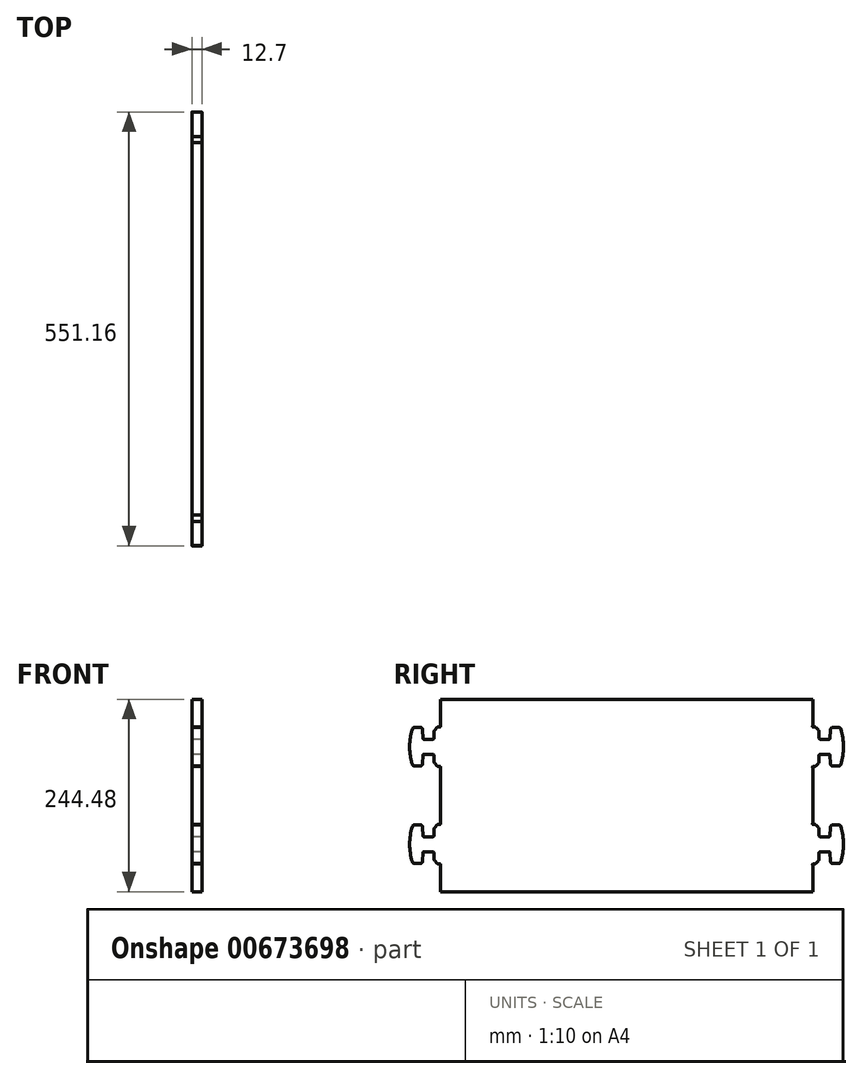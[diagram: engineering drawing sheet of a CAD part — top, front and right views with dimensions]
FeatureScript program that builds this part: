
annotation { "Feature Type Name" : "Feature", "Feature Type Description" : "" }
export const myFeature = defineFeature(function(context is Context, id is Id, definition is map)
    precondition{}
    {
        {
            var Q0;
            Q0=qCreatedBy(makeId("Right.planeOp"),FACE);
            var sketch = newSketch(context, id + "F0", { "sketchPlane" : qUnion([Q0])});
            skLineSegment(sketch, "E0", {"start": v(236.54, -75.4) * mm, "end": v(236.54, -109.14) * mm});
            skLineSegment(sketch, "E1", {"start": v(236.54, -109.14) * mm, "end": v(-236.54, -109.14) * mm});
            skLineSegment(sketch, "E2", {"start": v(-236.54, -109.14) * mm, "end": v(-236.54, -75.4) * mm});
            skArc(sketch, "E3", {"start": v(-236.54, -75.4) * mm, "mid": v(-236.5, -75.19) * mm, "end": v(-236.42, -75) * mm});
            skArc(sketch, "E4", {"start": v(-236.42, -75) * mm, "mid": v(-236.31, -74.48) * mm, "end": v(-236.54, -74.02) * mm});
            skArc(sketch, "E5", {"start": v(-236.54, -74.02) * mm, "mid": v(-237, -73.79) * mm, "end": v(-237.51, -73.9) * mm});
            skArc(sketch, "E6", {"start": v(-237.51, -73.9) * mm, "mid": v(-237.71, -73.99) * mm, "end": v(-237.93, -74.02) * mm});
            skLineSegment(sketch, "E7", {"start": v(-237.93, -74.02) * mm, "end": v(-238.4, -74.02) * mm});
            skArc(sketch, "E8", {"start": v(-238.4, -74.02) * mm, "mid": v(-239.61, -73.77) * mm, "end": v(-240.64, -73.09) * mm});
            skLineSegment(sketch, "E9", {"start": v(-240.64, -73.09) * mm, "end": v(-243.55, -70.18) * mm});
            skArc(sketch, "E10", {"start": v(-243.55, -70.18) * mm, "mid": v(-244.23, -69.15) * mm, "end": v(-244.48, -67.94) * mm});
            skLineSegment(sketch, "E11", {"start": v(-244.48, -67.94) * mm, "end": v(-244.48, -59.93) * mm});
            skArc(sketch, "E12", {"start": v(-244.48, -59.93) * mm, "mid": v(-244.94, -58.8) * mm, "end": v(-246.06, -58.34) * mm});
            skLineSegment(sketch, "E13", {"start": v(-246.06, -58.34) * mm, "end": v(-257.61, -58.34) * mm});
            skArc(sketch, "E14", {"start": v(-257.61, -58.34) * mm, "mid": v(-258.16, -58.56) * mm, "end": v(-258.4, -59.1) * mm});
            skLineSegment(sketch, "E15", {"start": v(-258.4, -59.1) * mm, "end": v(-259, -70.41) * mm});
            skArc(sketch, "E16", {"start": v(-259, -70.41) * mm, "mid": v(-259.99, -72.55) * mm, "end": v(-262.17, -73.42) * mm});
            skLineSegment(sketch, "E17", {"start": v(-262.17, -73.42) * mm, "end": v(-269.16, -73.42) * mm});
            skArc(sketch, "E18", {"start": v(-269.16, -73.42) * mm, "mid": v(-271.04, -72.8) * mm, "end": v(-272.2, -71.19) * mm});
            skArc(sketch, "E19", {"start": v(-272.2, -71.19) * mm, "mid": v(-275.58, -48.81) * mm, "end": v(-272.2, -26.44) * mm});
            skArc(sketch, "E20", {"start": v(-272.2, -26.44) * mm, "mid": v(-271.04, -24.83) * mm, "end": v(-269.16, -24.2) * mm});
            skLineSegment(sketch, "E21", {"start": v(-269.16, -24.2) * mm, "end": v(-262.17, -24.2) * mm});
            skArc(sketch, "E22", {"start": v(-262.17, -24.2) * mm, "mid": v(-259.99, -25.08) * mm, "end": v(-259, -27.22) * mm});
            skLineSegment(sketch, "E23", {"start": v(-259, -27.22) * mm, "end": v(-258.4, -38.54) * mm});
            skArc(sketch, "E24", {"start": v(-258.4, -38.54) * mm, "mid": v(-258.16, -39.07) * mm, "end": v(-257.61, -39.29) * mm});
            skLineSegment(sketch, "E25", {"start": v(-257.61, -39.29) * mm, "end": v(-246.06, -39.29) * mm});
            skArc(sketch, "E26", {"start": v(-246.06, -39.29) * mm, "mid": v(-244.94, -38.82) * mm, "end": v(-244.48, -37.7) * mm});
            skLineSegment(sketch, "E27", {"start": v(-244.48, -37.7) * mm, "end": v(-244.48, -29.69) * mm});
            skArc(sketch, "E28", {"start": v(-244.48, -29.69) * mm, "mid": v(-244.23, -28.47) * mm, "end": v(-243.55, -27.44) * mm});
            skLineSegment(sketch, "E29", {"start": v(-243.55, -27.44) * mm, "end": v(-240.64, -24.54) * mm});
            skArc(sketch, "E30", {"start": v(-240.64, -24.54) * mm, "mid": v(-239.61, -23.85) * mm, "end": v(-238.4, -23.61) * mm});
            skLineSegment(sketch, "E31", {"start": v(-238.4, -23.61) * mm, "end": v(-237.93, -23.61) * mm});
            skArc(sketch, "E32", {"start": v(-237.93, -23.61) * mm, "mid": v(-237.71, -23.64) * mm, "end": v(-237.51, -23.73) * mm});
            skArc(sketch, "E33", {"start": v(-237.51, -23.73) * mm, "mid": v(-236.54, -23.61) * mm, "end": v(-236.42, -22.64) * mm});
            skArc(sketch, "E34", {"start": v(-236.42, -22.64) * mm, "mid": v(-236.5, -22.44) * mm, "end": v(-236.54, -22.22) * mm});
            skLineSegment(sketch, "E35", {"start": v(-236.54, -22.22) * mm, "end": v(-236.54, 48.42) * mm});
            skArc(sketch, "E36", {"start": v(-236.54, 48.42) * mm, "mid": v(-236.5, 48.64) * mm, "end": v(-236.42, 48.83) * mm});
            skArc(sketch, "E37", {"start": v(-236.42, 48.83) * mm, "mid": v(-236.54, 49.8) * mm, "end": v(-237.51, 49.93) * mm});
            skArc(sketch, "E38", {"start": v(-237.51, 49.93) * mm, "mid": v(-237.71, 49.84) * mm, "end": v(-237.93, 49.8) * mm});
            skLineSegment(sketch, "E39", {"start": v(-237.93, 49.8) * mm, "end": v(-238.4, 49.8) * mm});
            skArc(sketch, "E40", {"start": v(-238.4, 49.8) * mm, "mid": v(-239.61, 50.05) * mm, "end": v(-240.64, 50.74) * mm});
            skLineSegment(sketch, "E41", {"start": v(-240.64, 50.74) * mm, "end": v(-243.55, 53.64) * mm});
            skArc(sketch, "E42", {"start": v(-243.55, 53.64) * mm, "mid": v(-244.23, 54.67) * mm, "end": v(-244.48, 55.89) * mm});
            skLineSegment(sketch, "E43", {"start": v(-244.48, 55.89) * mm, "end": v(-244.48, 63.9) * mm});
            skArc(sketch, "E44", {"start": v(-244.48, 63.9) * mm, "mid": v(-244.94, 65.02) * mm, "end": v(-246.06, 65.49) * mm});
            skLineSegment(sketch, "E45", {"start": v(-246.06, 65.49) * mm, "end": v(-257.61, 65.49) * mm});
            skArc(sketch, "E46", {"start": v(-257.61, 65.49) * mm, "mid": v(-258.16, 65.27) * mm, "end": v(-258.4, 64.73) * mm});
            skLineSegment(sketch, "E47", {"start": v(-258.4, 64.73) * mm, "end": v(-259, 53.41) * mm});
            skArc(sketch, "E48", {"start": v(-259, 53.41) * mm, "mid": v(-259.99, 51.28) * mm, "end": v(-262.17, 50.4) * mm});
            skLineSegment(sketch, "E49", {"start": v(-262.17, 50.4) * mm, "end": v(-269.16, 50.4) * mm});
            skArc(sketch, "E50", {"start": v(-269.16, 50.4) * mm, "mid": v(-271.04, 51.02) * mm, "end": v(-272.2, 52.64) * mm});
            skArc(sketch, "E51", {"start": v(-272.2, 52.64) * mm, "mid": v(-274.73, 63.7) * mm, "end": v(-275.53, 75.01) * mm});
            skArc(sketch, "E52", {"start": v(-275.53, 75.01) * mm, "mid": v(-274.68, 86.32) * mm, "end": v(-272.2, 97.38) * mm});
            skArc(sketch, "E53", {"start": v(-272.2, 97.38) * mm, "mid": v(-271.04, 99) * mm, "end": v(-269.16, 99.62) * mm});
            skLineSegment(sketch, "E54", {"start": v(-269.16, 99.62) * mm, "end": v(-262.17, 99.62) * mm});
            skArc(sketch, "E55", {"start": v(-262.17, 99.62) * mm, "mid": v(-259.99, 98.75) * mm, "end": v(-259, 96.6) * mm});
            skLineSegment(sketch, "E56", {"start": v(-259, 96.6) * mm, "end": v(-258.4, 85.29) * mm});
            skArc(sketch, "E57", {"start": v(-258.4, 85.29) * mm, "mid": v(-258.16, 84.75) * mm, "end": v(-257.61, 84.54) * mm});
            skLineSegment(sketch, "E58", {"start": v(-257.61, 84.54) * mm, "end": v(-246.06, 84.54) * mm});
            skArc(sketch, "E59", {"start": v(-246.06, 84.54) * mm, "mid": v(-244.94, 85) * mm, "end": v(-244.48, 86.12) * mm});
            skLineSegment(sketch, "E60", {"start": v(-244.48, 86.12) * mm, "end": v(-244.48, 94.14) * mm});
            skArc(sketch, "E61", {"start": v(-244.48, 94.14) * mm, "mid": v(-244.23, 95.35) * mm, "end": v(-243.55, 96.38) * mm});
            skLineSegment(sketch, "E62", {"start": v(-243.55, 96.38) * mm, "end": v(-240.64, 99.28) * mm});
            skArc(sketch, "E63", {"start": v(-240.64, 99.28) * mm, "mid": v(-239.61, 99.97) * mm, "end": v(-238.4, 100.21) * mm});
            skLineSegment(sketch, "E64", {"start": v(-238.4, 100.21) * mm, "end": v(-237.93, 100.21) * mm});
            skArc(sketch, "E65", {"start": v(-237.93, 100.21) * mm, "mid": v(-237.71, 100.18) * mm, "end": v(-237.51, 100.1) * mm});
            skArc(sketch, "E66", {"start": v(-237.51, 100.1) * mm, "mid": v(-237, 99.99) * mm, "end": v(-236.54, 100.21) * mm});
            skArc(sketch, "E67", {"start": v(-236.54, 100.21) * mm, "mid": v(-236.31, 100.68) * mm, "end": v(-236.42, 101.19) * mm});
            skArc(sketch, "E68", {"start": v(-236.42, 101.19) * mm, "mid": v(-236.5, 101.39) * mm, "end": v(-236.54, 101.6) * mm});
            skLineSegment(sketch, "E69", {"start": v(-236.54, 101.6) * mm, "end": v(-236.54, 135.34) * mm});
            skLineSegment(sketch, "E70", {"start": v(-236.54, 135.34) * mm, "end": v(236.54, 135.34) * mm});
            skLineSegment(sketch, "E71", {"start": v(236.54, 135.34) * mm, "end": v(236.54, 101.6) * mm});
            skArc(sketch, "E72", {"start": v(236.54, 101.6) * mm, "mid": v(236.5, 101.39) * mm, "end": v(236.42, 101.19) * mm});
            skArc(sketch, "E73", {"start": v(236.42, 101.19) * mm, "mid": v(236.31, 100.68) * mm, "end": v(236.54, 100.21) * mm});
            skArc(sketch, "E74", {"start": v(236.54, 100.21) * mm, "mid": v(237, 99.99) * mm, "end": v(237.51, 100.1) * mm});
            skArc(sketch, "E75", {"start": v(237.51, 100.1) * mm, "mid": v(237.71, 100.18) * mm, "end": v(237.93, 100.21) * mm});
            skLineSegment(sketch, "E76", {"start": v(237.93, 100.21) * mm, "end": v(238.4, 100.21) * mm});
            skArc(sketch, "E77", {"start": v(238.4, 100.21) * mm, "mid": v(239.61, 99.97) * mm, "end": v(240.64, 99.28) * mm});
            skLineSegment(sketch, "E78", {"start": v(240.64, 99.28) * mm, "end": v(243.55, 96.38) * mm});
            skArc(sketch, "E79", {"start": v(243.55, 96.38) * mm, "mid": v(244.23, 95.35) * mm, "end": v(244.48, 94.14) * mm});
            skLineSegment(sketch, "E80", {"start": v(244.48, 94.14) * mm, "end": v(244.48, 86.12) * mm});
            skArc(sketch, "E81", {"start": v(244.48, 86.12) * mm, "mid": v(244.94, 85) * mm, "end": v(246.06, 84.54) * mm});
            skLineSegment(sketch, "E82", {"start": v(246.06, 84.54) * mm, "end": v(257.61, 84.54) * mm});
            skArc(sketch, "E83", {"start": v(257.61, 84.54) * mm, "mid": v(258.16, 84.75) * mm, "end": v(258.4, 85.29) * mm});
            skLineSegment(sketch, "E84", {"start": v(258.4, 85.29) * mm, "end": v(259, 96.6) * mm});
            skArc(sketch, "E85", {"start": v(259, 96.6) * mm, "mid": v(259.99, 98.75) * mm, "end": v(262.17, 99.62) * mm});
            skLineSegment(sketch, "E86", {"start": v(262.17, 99.62) * mm, "end": v(269.16, 99.62) * mm});
            skArc(sketch, "E87", {"start": v(269.16, 99.62) * mm, "mid": v(271.04, 99) * mm, "end": v(272.2, 97.38) * mm});
            skArc(sketch, "E88", {"start": v(272.2, 97.38) * mm, "mid": v(275.58, 75.01) * mm, "end": v(272.2, 52.64) * mm});
            skArc(sketch, "E89", {"start": v(272.2, 52.64) * mm, "mid": v(271.04, 51.02) * mm, "end": v(269.16, 50.4) * mm});
            skLineSegment(sketch, "E90", {"start": v(269.16, 50.4) * mm, "end": v(262.17, 50.4) * mm});
            skArc(sketch, "E91", {"start": v(262.17, 50.4) * mm, "mid": v(259.99, 51.28) * mm, "end": v(259, 53.41) * mm});
            skLineSegment(sketch, "E92", {"start": v(259, 53.41) * mm, "end": v(258.4, 64.73) * mm});
            skArc(sketch, "E93", {"start": v(258.4, 64.73) * mm, "mid": v(258.16, 65.27) * mm, "end": v(257.61, 65.49) * mm});
            skLineSegment(sketch, "E94", {"start": v(257.61, 65.49) * mm, "end": v(246.06, 65.49) * mm});
            skArc(sketch, "E95", {"start": v(246.06, 65.49) * mm, "mid": v(244.94, 65.02) * mm, "end": v(244.48, 63.9) * mm});
            skLineSegment(sketch, "E96", {"start": v(244.48, 63.9) * mm, "end": v(244.48, 55.89) * mm});
            skArc(sketch, "E97", {"start": v(244.48, 55.89) * mm, "mid": v(244.23, 54.67) * mm, "end": v(243.55, 53.64) * mm});
            skLineSegment(sketch, "E98", {"start": v(243.55, 53.64) * mm, "end": v(240.64, 50.74) * mm});
            skArc(sketch, "E99", {"start": v(240.64, 50.74) * mm, "mid": v(239.61, 50.05) * mm, "end": v(238.4, 49.8) * mm});
            skLineSegment(sketch, "E100", {"start": v(238.4, 49.8) * mm, "end": v(237.93, 49.8) * mm});
            skArc(sketch, "E101", {"start": v(237.93, 49.8) * mm, "mid": v(237.71, 49.84) * mm, "end": v(237.51, 49.93) * mm});
            skArc(sketch, "E102", {"start": v(237.51, 49.93) * mm, "mid": v(236.54, 49.8) * mm, "end": v(236.42, 48.83) * mm});
            skArc(sketch, "E103", {"start": v(236.42, 48.83) * mm, "mid": v(236.5, 48.64) * mm, "end": v(236.54, 48.42) * mm});
            skLineSegment(sketch, "E104", {"start": v(236.54, 48.42) * mm, "end": v(236.54, -22.22) * mm});
            skArc(sketch, "E105", {"start": v(236.54, -22.22) * mm, "mid": v(236.5, -22.44) * mm, "end": v(236.42, -22.64) * mm});
            skArc(sketch, "E106", {"start": v(236.42, -22.64) * mm, "mid": v(236.54, -23.61) * mm, "end": v(237.51, -23.73) * mm});
            skArc(sketch, "E107", {"start": v(237.51, -23.73) * mm, "mid": v(237.71, -23.64) * mm, "end": v(237.93, -23.61) * mm});
            skLineSegment(sketch, "E108", {"start": v(237.93, -23.61) * mm, "end": v(238.4, -23.61) * mm});
            skArc(sketch, "E109", {"start": v(238.4, -23.61) * mm, "mid": v(239.61, -23.85) * mm, "end": v(240.64, -24.54) * mm});
            skLineSegment(sketch, "E110", {"start": v(240.64, -24.54) * mm, "end": v(243.55, -27.44) * mm});
            skArc(sketch, "E111", {"start": v(243.55, -27.44) * mm, "mid": v(244.23, -28.47) * mm, "end": v(244.48, -29.69) * mm});
            skLineSegment(sketch, "E112", {"start": v(244.48, -29.69) * mm, "end": v(244.48, -37.7) * mm});
            skArc(sketch, "E113", {"start": v(244.48, -37.7) * mm, "mid": v(244.94, -38.82) * mm, "end": v(246.06, -39.29) * mm});
            skLineSegment(sketch, "E114", {"start": v(246.06, -39.29) * mm, "end": v(257.61, -39.29) * mm});
            skArc(sketch, "E115", {"start": v(257.61, -39.29) * mm, "mid": v(258.16, -39.07) * mm, "end": v(258.4, -38.54) * mm});
            skLineSegment(sketch, "E116", {"start": v(258.4, -38.54) * mm, "end": v(259, -27.22) * mm});
            skArc(sketch, "E117", {"start": v(259, -27.22) * mm, "mid": v(259.99, -25.08) * mm, "end": v(262.17, -24.2) * mm});
            skLineSegment(sketch, "E118", {"start": v(262.17, -24.2) * mm, "end": v(269.16, -24.2) * mm});
            skArc(sketch, "E119", {"start": v(269.16, -24.2) * mm, "mid": v(271.04, -24.83) * mm, "end": v(272.2, -26.44) * mm});
            skArc(sketch, "E120", {"start": v(272.2, -26.44) * mm, "mid": v(275.58, -48.81) * mm, "end": v(272.2, -71.19) * mm});
            skArc(sketch, "E121", {"start": v(272.2, -71.19) * mm, "mid": v(271.04, -72.8) * mm, "end": v(269.16, -73.42) * mm});
            skLineSegment(sketch, "E122", {"start": v(269.16, -73.42) * mm, "end": v(262.17, -73.42) * mm});
            skArc(sketch, "E123", {"start": v(262.17, -73.42) * mm, "mid": v(259.99, -72.55) * mm, "end": v(259, -70.41) * mm});
            skLineSegment(sketch, "E124", {"start": v(259, -70.41) * mm, "end": v(258.4, -59.1) * mm});
            skArc(sketch, "E125", {"start": v(258.4, -59.1) * mm, "mid": v(258.16, -58.56) * mm, "end": v(257.61, -58.34) * mm});
            skLineSegment(sketch, "E126", {"start": v(257.61, -58.34) * mm, "end": v(246.06, -58.34) * mm});
            skArc(sketch, "E127", {"start": v(246.06, -58.34) * mm, "mid": v(244.94, -58.8) * mm, "end": v(244.48, -59.93) * mm});
            skLineSegment(sketch, "E128", {"start": v(244.48, -59.93) * mm, "end": v(244.48, -67.94) * mm});
            skArc(sketch, "E129", {"start": v(244.48, -67.94) * mm, "mid": v(244.23, -69.15) * mm, "end": v(243.55, -70.18) * mm});
            skLineSegment(sketch, "E130", {"start": v(243.55, -70.18) * mm, "end": v(240.64, -73.09) * mm});
            skArc(sketch, "E131", {"start": v(240.64, -73.09) * mm, "mid": v(239.61, -73.77) * mm, "end": v(238.4, -74.02) * mm});
            skLineSegment(sketch, "E132", {"start": v(238.4, -74.02) * mm, "end": v(237.93, -74.02) * mm});
            skArc(sketch, "E133", {"start": v(237.93, -74.02) * mm, "mid": v(237.71, -73.99) * mm, "end": v(237.51, -73.9) * mm});
            skArc(sketch, "E134", {"start": v(237.51, -73.9) * mm, "mid": v(237, -73.79) * mm, "end": v(236.54, -74.02) * mm});
            skArc(sketch, "E135", {"start": v(236.54, -74.02) * mm, "mid": v(236.31, -74.48) * mm, "end": v(236.42, -75) * mm});
            skArc(sketch, "E136", {"start": v(236.42, -75) * mm, "mid": v(236.5, -75.19) * mm, "end": v(236.54, -75.4) * mm});
            skSolve(sketch);
        }
        {
            var Q0;
            Q0=makeQuery(id+"F0.imprint","IMPRINT",FACE,{"disambiguationData":[TD([[makeQuery(id+"F0.imprint","IMPRINT",EDGE,{"derivedFrom":sQuery(id+"F0.wireOp",EDGE,"E0")}),-1.0]])]});
            extrude(context, id + "F1", {"entities" : qUnion([Q0]), "depth" : 12.7 * mm, "offsetDistance" : 25.4 * mm});
        }
    });
